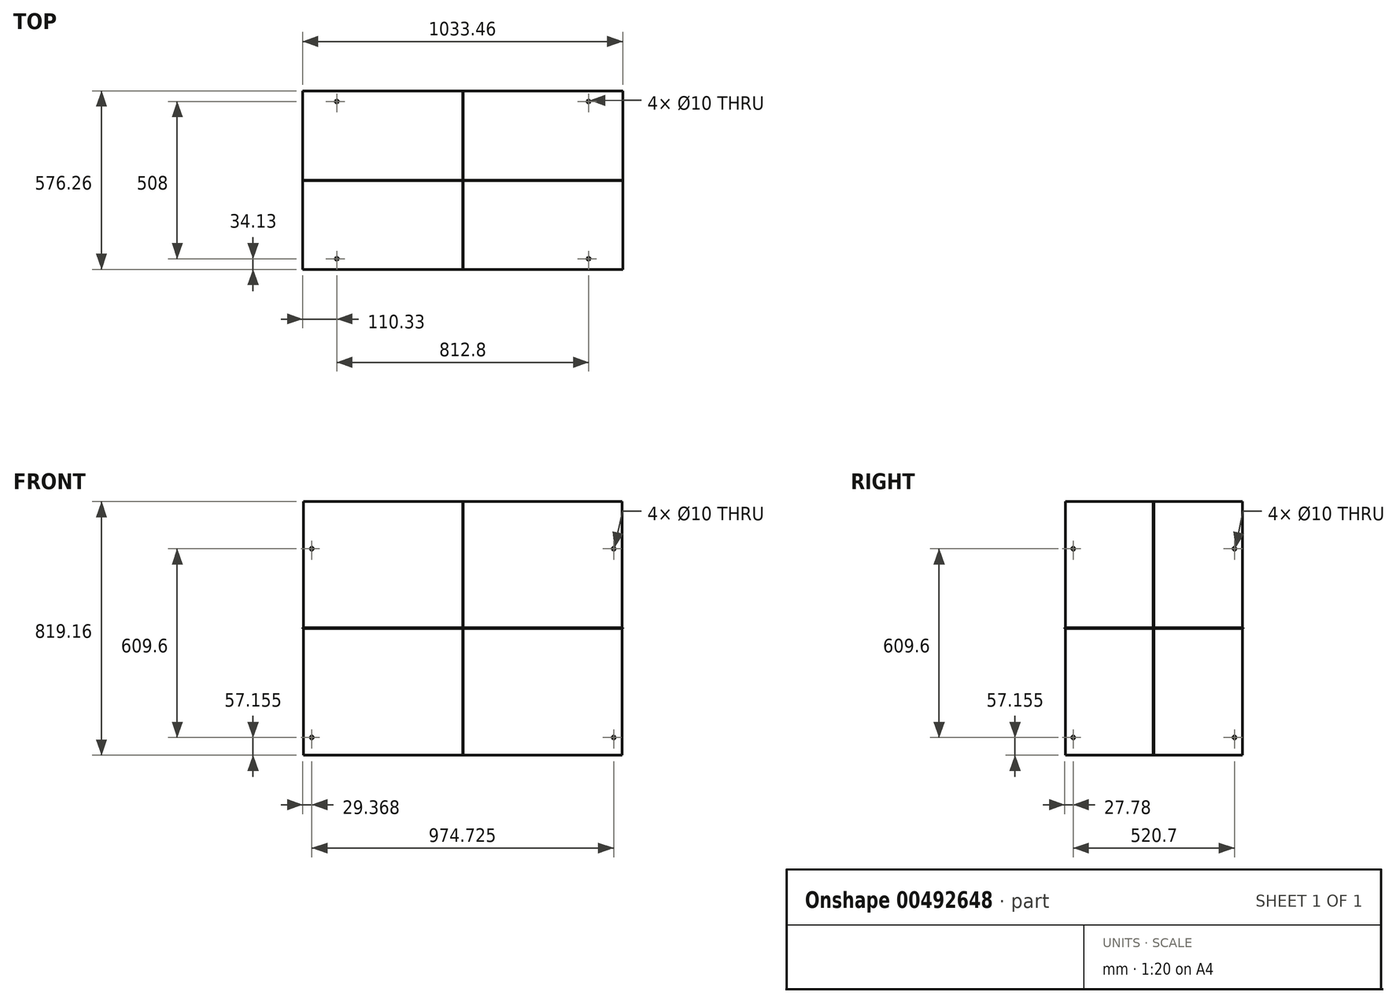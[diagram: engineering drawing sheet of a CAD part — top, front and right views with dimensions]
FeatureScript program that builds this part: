
annotation { "Feature Type Name" : "Feature", "Feature Type Description" : "" }
export const myFeature = defineFeature(function(context is Context, id is Id, definition is map)
    precondition{}
    {
        {
            var Q0;
            Q0=qCreatedBy(makeId("Right.planeOp"),FACE);
            var sketch = newSketch(context, id + "F0", { "sketchPlane" : qUnion([Q0])});
            skLineSegment(sketch, "E0.bottom", {"start": v(285.75, -409.58) * mm, "end": v(-285.75, -409.58) * mm});
            skLineSegment(sketch, "E0.top", {"start": v(285.75, 409.58) * mm, "end": v(-285.75, 409.58) * mm});
            skLineSegment(sketch, "E0.left", {"start": v(285.75, -409.58) * mm, "end": v(285.75, 409.58) * mm});
            skLineSegment(sketch, "E0.right", {"start": v(-285.75, -409.58) * mm, "end": v(-285.75, 409.58) * mm});
            skPoint(sketch, "E0.middle", {"position": v(0, 0) * mm});
            skSolve(sketch);
        }
        {
            var Q0;
            Q0 = qSketchRegion(id + "F0", true);
            extrude(context, id + "F1", {"entities" : qUnion([Q0]), "depth" : 1.9 * mm, "offsetDistance" : 25 * mm});
        }
        {
            var Q0;
            Q0=makeQuery(id+"F1.opExtrude","CAP_FACE",FACE,{"disambiguationData":[OSD([sQuery(id+"F0.wireOp",EDGE,"E0.bottom"),sQuery(id+"F0.wireOp",EDGE,"E0.top"),sQuery(id+"F0.wireOp",EDGE,"E0.left"),sQuery(id+"F0.wireOp",EDGE,"E0.right")])],"isStart":false});
            var sketch = newSketch(context, id + "F2", { "sketchPlane" : qUnion([Q0])});
            skCircle(sketch, "E1", {"center": v(-260.35, 257.18) * mm, "radius": 5 * mm});
            skLineSegment(sketch, "E2", {"start": v(0, 409.58) * mm, "end": v(0, -409.58) * mm, "construction": true});
            skLineSegment(sketch, "E3", {"start": v(-285.75, 0) * mm, "end": v(285.75, 0) * mm, "construction": true});
            skCircle(sketch, "E4", {"center": v(-260.35, -352.43) * mm, "radius": 5 * mm});
            skCircle(sketch, "E5.MirrorC", {"center": v(260.35, 257.18) * mm, "radius": 5 * mm});
            skCircle(sketch, "E6.MirrorC", {"center": v(260.35, -352.42) * mm, "radius": 5 * mm});
            skSolve(sketch);
        }
        {
            var Q0;
            Q0 = qSketchRegion(id + "F2", true);
            extrude(context, id + "F3", {"entities" : qUnion([Q0]), "operationType" : NewBodyOperationType.REMOVE, "endBound" : BoundingType.THROUGH_ALL, "oppositeDirection" : true, "depth" : 25 * mm, "offsetDistance" : 25 * mm});
        }
        {
            var Q0;
            Q0=qCreatedBy(makeId("Front.planeOp"),FACE);
            var sketch = newSketch(context, id + "F4", { "sketchPlane" : qUnion([Q0])});
            skLineSegment(sketch, "E7.bottom", {"start": v(514.35, -409.58) * mm, "end": v(-514.35, -409.58) * mm});
            skLineSegment(sketch, "E7.top", {"start": v(514.35, 409.58) * mm, "end": v(-514.35, 409.58) * mm});
            skLineSegment(sketch, "E7.left", {"start": v(514.35, -409.58) * mm, "end": v(514.35, 409.58) * mm});
            skLineSegment(sketch, "E7.right", {"start": v(-514.35, -409.58) * mm, "end": v(-514.35, 409.58) * mm});
            skPoint(sketch, "E7.middle", {"position": v(0, 0) * mm});
            skSolve(sketch);
        }
        {
            var Q0;
            Q0 = qSketchRegion(id + "F4", true);
            extrude(context, id + "F5", {"entities" : qUnion([Q0]), "depth" : 1.9 * mm, "offsetDistance" : 25 * mm});
        }
        {
            var Q0;
            Q0=makeQuery(id+"F5.opExtrude","CAP_FACE",FACE,{"disambiguationData":[OSD([sQuery(id+"F4.wireOp",EDGE,"E7.bottom"),sQuery(id+"F4.wireOp",EDGE,"E7.top"),sQuery(id+"F4.wireOp",EDGE,"E7.left"),sQuery(id+"F4.wireOp",EDGE,"E7.right")])],"isStart":false});
            var sketch = newSketch(context, id + "F6", { "sketchPlane" : qUnion([Q0])});
            skLineSegment(sketch, "E8", {"start": v(0, 409.58) * mm, "end": v(0, -409.58) * mm, "construction": true});
            skLineSegment(sketch, "E9", {"start": v(-514.35, 0) * mm, "end": v(514.35, 0) * mm, "construction": true});
            skCircle(sketch, "E10", {"center": v(-487.36, 257.18) * mm, "radius": 5 * mm});
            skCircle(sketch, "E11.MirrorC", {"center": v(487.36, 257.17) * mm, "radius": 5 * mm});
            skCircle(sketch, "E12.MirrorC", {"center": v(-487.36, -352.43) * mm, "radius": 5 * mm});
            skCircle(sketch, "E13.MirrorC", {"center": v(487.36, -352.43) * mm, "radius": 5 * mm});
            skLineSegment(sketch, "E14", {"start": v(-487.36, -352.43) * mm, "end": v(487.36, -352.43) * mm, "construction": true});
            skLineSegment(sketch, "E15", {"start": v(-487.36, 257.18) * mm, "end": v(487.36, 257.17) * mm, "construction": true});
            skLineSegment(sketch, "E16", {"start": v(-487.36, -352.43) * mm, "end": v(-487.36, 257.18) * mm, "construction": true});
            skSolve(sketch);
        }
        {
            var Q0;
            Q0 = qSketchRegion(id + "F6", true);
            extrude(context, id + "F7", {"entities" : qUnion([Q0]), "operationType" : NewBodyOperationType.REMOVE, "endBound" : BoundingType.THROUGH_ALL, "oppositeDirection" : true, "depth" : 25 * mm, "offsetDistance" : 25 * mm});
        }
        {
            var Q0;
            Q0=qCreatedBy(makeId("Top.planeOp"),FACE);
            var sketch = newSketch(context, id + "F8", { "sketchPlane" : qUnion([Q0])});
            skLineSegment(sketch, "E17.bottom", {"start": v(516.73, -288.13) * mm, "end": v(-516.73, -288.13) * mm});
            skLineSegment(sketch, "E17.top", {"start": v(516.73, 288.13) * mm, "end": v(-516.73, 288.13) * mm});
            skLineSegment(sketch, "E17.left", {"start": v(516.73, -288.13) * mm, "end": v(516.73, 288.13) * mm});
            skLineSegment(sketch, "E17.right", {"start": v(-516.73, -288.13) * mm, "end": v(-516.73, 288.13) * mm});
            skPoint(sketch, "E17.middle", {"position": v(0, 0) * mm});
            skSolve(sketch);
        }
        {
            var Q0;
            Q0 = qSketchRegion(id + "F8", true);
            extrude(context, id + "F9", {"entities" : qUnion([Q0]), "depth" : 1.9 * mm, "offsetDistance" : 25 * mm});
        }
        {
            var Q0;
            Q0=makeQuery(id+"F9.opExtrude","CAP_FACE",FACE,{"disambiguationData":[OSD([sQuery(id+"F8.wireOp",EDGE,"E17.bottom"),sQuery(id+"F8.wireOp",EDGE,"E17.top"),sQuery(id+"F8.wireOp",EDGE,"E17.left"),sQuery(id+"F8.wireOp",EDGE,"E17.right")])],"isStart":false});
            var sketch = newSketch(context, id + "F10", { "sketchPlane" : qUnion([Q0])});
            skLineSegment(sketch, "E18", {"start": v(506.9, 0) * mm, "end": v(-515.93, 0) * mm, "construction": true});
            skLineSegment(sketch, "E19", {"start": v(0, -241.67) * mm, "end": v(0, 332.7) * mm, "construction": true});
            skCircle(sketch, "E20", {"center": v(406.4, -254) * mm, "radius": 5 * mm});
            skCircle(sketch, "E21", {"center": v(-406.4, -254) * mm, "radius": 5 * mm});
            skCircle(sketch, "E22", {"center": v(406.4, 254) * mm, "radius": 5 * mm});
            skCircle(sketch, "E23", {"center": v(-406.4, 254) * mm, "radius": 5 * mm});
            skLineSegment(sketch, "E24", {"start": v(-406.4, 254) * mm, "end": v(-406.4, -254) * mm, "construction": true});
            skLineSegment(sketch, "E25", {"start": v(-406.4, -254) * mm, "end": v(406.4, -254) * mm, "construction": true});
            skLineSegment(sketch, "E26", {"start": v(406.4, -254) * mm, "end": v(406.4, 254) * mm, "construction": true});
            skLineSegment(sketch, "E27", {"start": v(-406.4, 254) * mm, "end": v(406.4, 254) * mm, "construction": true});
            skSolve(sketch);
        }
        {
            var Q0;
            Q0 = qSketchRegion(id + "F10", true);
            extrude(context, id + "F11", {"entities" : qUnion([Q0]), "operationType" : NewBodyOperationType.REMOVE, "endBound" : BoundingType.THROUGH_ALL, "oppositeDirection" : true, "depth" : 25 * mm, "offsetDistance" : 25 * mm});
        }
    });
